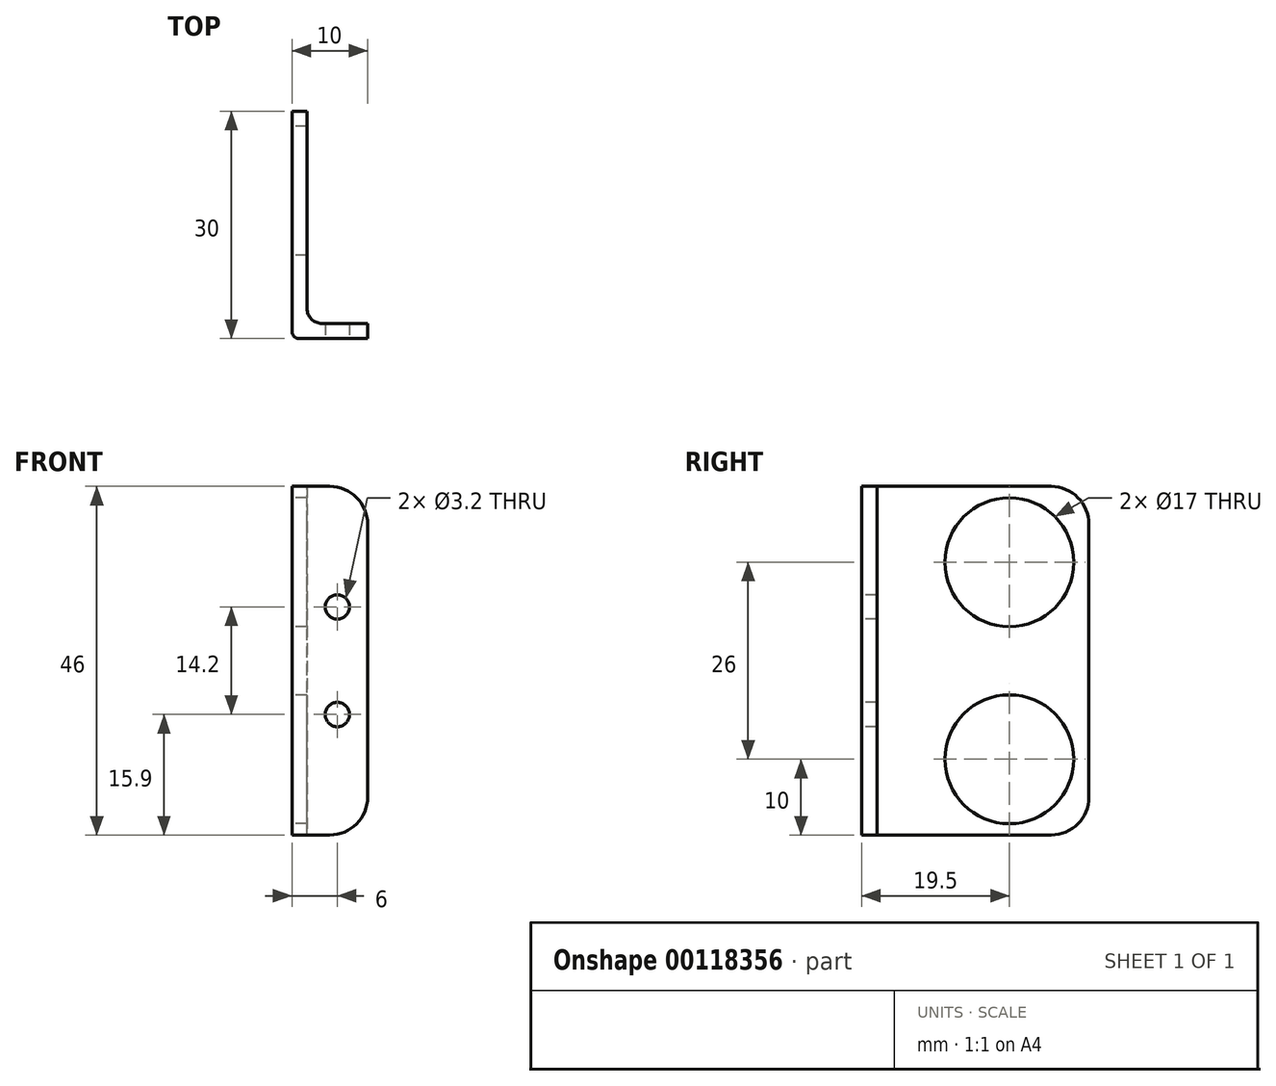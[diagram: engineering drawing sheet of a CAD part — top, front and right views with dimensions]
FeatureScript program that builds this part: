
annotation { "Feature Type Name" : "Feature", "Feature Type Description" : "" }
export const myFeature = defineFeature(function(context is Context, id is Id, definition is map)
    precondition{}
    {
        {
            var Q0;
            Q0=qCreatedBy(makeId("Right.planeOp"),FACE);
            var sketch = newSketch(context, id + "F0", { "sketchPlane" : qUnion([Q0])});
            skLineSegment(sketch, "E0.bottom", {"start": v(0, 0) * mm, "end": v(30, 0) * mm});
            skLineSegment(sketch, "E0.top", {"start": v(0, 46) * mm, "end": v(30, 46) * mm});
            skLineSegment(sketch, "E0.left", {"start": v(0, 0) * mm, "end": v(0, 46) * mm});
            skLineSegment(sketch, "E0.right", {"start": v(30, 0) * mm, "end": v(30, 46) * mm});
            skLineSegment(sketch, "E1.0", {"start": v(28, 0) * mm, "end": v(28, 46) * mm, "construction": true});
            skLineSegment(sketch, "E2.0", {"start": v(0, 1.5) * mm, "end": v(30, 1.5) * mm, "construction": true});
            skLineSegment(sketch, "E3.0", {"start": v(0, 44.5) * mm, "end": v(30, 44.5) * mm, "construction": true});
            skLineSegment(sketch, "E4.0", {"start": v(0, 10) * mm, "end": v(30, 10) * mm, "construction": true});
            skLineSegment(sketch, "E5.0", {"start": v(0, 36) * mm, "end": v(30, 36) * mm, "construction": true});
            skLineSegment(sketch, "E6.0", {"start": v(19.5, 0) * mm, "end": v(19.5, 46) * mm, "construction": true});
            skCircle(sketch, "E7", {"center": v(19.5, 36) * mm, "radius": 8.5 * mm});
            skCircle(sketch, "E8", {"center": v(19.5, 10) * mm, "radius": 8.5 * mm});
            skSolve(sketch);
        }
        {
            var Q0;
            Q0=makeQuery(id+"F0.imprint","IMPRINT",FACE,{"disambiguationData":[TD([[makeQuery(id+"F0.imprint","IMPRINT",EDGE,{"derivedFrom":sQuery(id+"F0.wireOp",EDGE,"E0.bottom")}),1.0]])]});
            extrude(context, id + "F1", {"entities" : qUnion([Q0]), "depth" : 2 * mm});
        }
        {
            var Q0;
            Q0=makeQuery(id+"F1.opExtrude","SWEPT_FACE",FACE,{"disambiguationData":[OSD([sQuery(id+"F0.wireOp",EDGE,"E0.top")])]});
            var sketch = newSketch(context, id + "F2", { "sketchPlane" : qUnion([Q0])});
            skLineSegment(sketch, "E9.bottom", {"start": v(0, 0) * mm, "end": v(10, 0) * mm});
            skLineSegment(sketch, "E9.top", {"start": v(0, 2) * mm, "end": v(10, 2) * mm});
            skLineSegment(sketch, "E9.left", {"start": v(0, 0) * mm, "end": v(0, 2) * mm});
            skLineSegment(sketch, "E9.right", {"start": v(10, 0) * mm, "end": v(10, 2) * mm});
            skSolve(sketch);
        }
        {
            var Q0;
            Q0 = qSketchRegion(id + "F2", true);
            extrude(context, id + "F3", {"entities" : qUnion([Q0]), "operationType" : NewBodyOperationType.ADD, "oppositeDirection" : true, "depth" : 46 * mm});
        }
        {
            var Q0;
            Q0=makeQuery(id+"F3.boolean.opBoolean","MERGE",FACE,{"derivedFrom":[makeQuery(id+"F1.opExtrude","SWEPT_FACE",FACE,{"disambiguationData":[OSD([sQuery(id+"F0.wireOp",EDGE,"E0.left")])]}),makeQuery(id+"F3.opExtrude","SWEPT_FACE",FACE,{"disambiguationData":[OSD([sQuery(id+"F2.wireOp",EDGE,"E9.bottom")])]})]});
            var sketch = newSketch(context, id + "F4", { "sketchPlane" : qUnion([Q0])});
            skLineSegment(sketch, "E10", {"start": v(10, 23) * mm, "end": v(0, 23) * mm, "construction": true});
            skLineSegment(sketch, "E11.0", {"start": v(10, 15.9) * mm, "end": v(0, 15.9) * mm, "construction": true});
            skLineSegment(sketch, "E12.0", {"start": v(10, 30.1) * mm, "end": v(0, 30.1) * mm, "construction": true});
            skLineSegment(sketch, "E13.0", {"start": v(6, 0) * mm, "end": v(6, 46) * mm, "construction": true});
            skCircle(sketch, "E14", {"center": v(6, 30.1) * mm, "radius": 1.6 * mm});
            skCircle(sketch, "E15", {"center": v(6, 15.9) * mm, "radius": 1.6 * mm});
            skSolve(sketch);
        }
        {
            var Q0;
            Q0 = qSketchRegion(id + "F4", true);
            extrude(context, id + "F5", {"entities" : qUnion([Q0]), "operationType" : NewBodyOperationType.REMOVE, "oppositeDirection" : true, "depth" : 25 * mm});
        }
        {
            var Q0;
            Q0=makeQuery(id+"F1.opExtrude","CAP_EDGE",EDGE,{"disambiguationData":[OSD([sQuery(id+"F0.wireOp",EDGE,"E0.left")])],"isStart":true});
            fillet(context, id + "F6", {"entities" : qUnion([Q0]), "radius" : 1 * mm, "tangentPropagation" : true, "allowEdgeOverflow" : false});
        }
        {
            var Q0;
            Q0=makeQuery(id+"F3.boolean.opBoolean","INTERSECT",EDGE,{"derivedFrom":[makeQuery(id+"F1.opExtrude","CAP_FACE",FACE,{"disambiguationData":[OSD([sQuery(id+"F0.wireOp",EDGE,"E0.bottom"),sQuery(id+"F0.wireOp",EDGE,"E0.top"),sQuery(id+"F0.wireOp",EDGE,"E0.left"),sQuery(id+"F0.wireOp",EDGE,"E0.right"),sQuery(id+"F0.wireOp",EDGE,"E7"),sQuery(id+"F0.wireOp",EDGE,"E8")])],"isStart":false}),makeQuery(id+"F3.opExtrude","SWEPT_FACE",FACE,{"disambiguationData":[OSD([sQuery(id+"F2.wireOp",EDGE,"E9.top")])]})]});
            fillet(context, id + "F7", {"entities" : qUnion([Q0]), "radius" : 2 * mm, "tangentPropagation" : true, "allowEdgeOverflow" : false});
        }
        {
            var Q0;
            Q0=makeQuery(id+"F1.opExtrude","SWEPT_EDGE",EDGE,{"disambiguationData":[OSD([sQuery(id+"F0.wireOp",EDGE,"E0.top"),sQuery(id+"F0.wireOp",EDGE,"E0.right")])]});
            fillet(context, id + "F8", {"entities" : qUnion([Q0]), "radius" : 5 * mm, "tangentPropagation" : true, "allowEdgeOverflow" : false});
        }
        {
            var Q0;
            Q0=makeQuery(id+"F1.opExtrude","SWEPT_EDGE",EDGE,{"disambiguationData":[OSD([sQuery(id+"F0.wireOp",EDGE,"E0.bottom"),sQuery(id+"F0.wireOp",EDGE,"E0.right")])]});
            var Q1;
            Q1=makeQuery(id+"F3.opExtrude","CAP_EDGE",EDGE,{"disambiguationData":[OSD([sQuery(id+"F2.wireOp",EDGE,"E9.right")])],"isStart":true});
            var Q2;
            Q2=makeQuery(id+"F3.opExtrude","CAP_EDGE",EDGE,{"disambiguationData":[OSD([sQuery(id+"F2.wireOp",EDGE,"E9.right")])],"isStart":false});
            fillet(context, id + "F9", {"entities" : qUnion([Q0, Q1, Q2]), "radius" : 5 * mm, "tangentPropagation" : true, "allowEdgeOverflow" : false});
        }
    });
